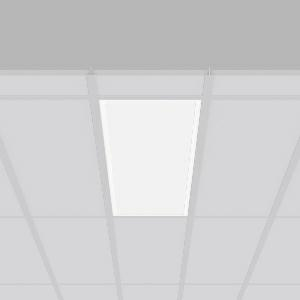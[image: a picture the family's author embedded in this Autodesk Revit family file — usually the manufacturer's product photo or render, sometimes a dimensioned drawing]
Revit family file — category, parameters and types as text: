
# Revit family: sidelite_eco_672372_002_1_04_6a0e
name_source: partatom
category: Lighting Fixtures
units: mm (PartAtom-declared; Revit-internal decimal feet)

## family parameters
Cut with Voids When Loaded = No
Host = Face
Light Source = No
Part Type = Normal
Room Calculation Point = No
Round Connector Dimension = Use Diameter
Shared = No

## types (1)
- SIDELITE ECO (1 x LED Modul 840, 3550 lm, 4000)
    Apparent Load = 29 VA
    CIE Flux Codes = 46 79 96 100 100
    Color Rendering = 80
    Color Temperature = 4000
    Default Elevation = 1800 mm
    Description = Series: SIDELITE ECO
Highly economical recessed luminaire with progressive LED technology. For escape route illumination. Frame made of aluminium, powder-coated. Diffuser: plastic, opal. Lightguide and diffuser made of non-yellowing plastic (PMMA). Lateral light emission (RZB SIDELITE technology) for homogeneous light distribution. External driver. Self-contained system with automatic self-test and feedback to the RZB monitoring system MULTIDIGIT. External driver with simple plug-in locking system. Extended connection cable (1.90 m). 
Colour: white
Length: 1195 mm
Width: 295 mm
Cut-out length: 1170 mm
Cut-out width: 270 mm
Recess height: 160 mm
Luminaire: recess height: 40 mm
Weight: 4.4 kg
Operating mode: maintained power mode
Duration time: 8 h
Lamp: LED
Socket: without socket
Colour temperature: 4000K
Colour rendering index (CRI): 80
System power: 29 W
Rated luminous flux: 3550 lm
Luminous flux, emergency: 240 lm
System power, emergency: -
Control gear: Regulated power supply
Protection class: I
Type of protection: IP 40
    Height = 0 mm  [stored 0 ft]
    Lamp = 1 x LED Modul 840
    Lamp Light Flux = 3550 lm
    Lamp count = 1
    Length = 1195 mm
    Lifetime = 50000 h
    Luminous efficacy = 122 lm/W
    Manufacturer = RZB
    ModVariant = No
    Model = 672372.002.1.04
    Mounting Place = Ceiling
    Mounting Type = Recessed
    Number of Poles = 1
    OnlyDefault = Yes
    Power Factor = 1
    Product Name = SIDELITE ECO
    Product group = Recessed modular luminaires
    ProductGroupID = 406
    Protection Class = Protection class I
    Protection Degree = IP 40
    RLX_Detail_Level = 1
    RLX_Emergency_Light_Flux = 240 lm
    RLX_Emergency_Type = 3
    RLX_Emergency_Type_DB = Yes
    RlxData = <blob elided: 30733 chars, md5=03e999d5>
    Socket = socket
    Standby Power = 0 W
    System Light Flux = 3550 lm
    System Power = 29 W
    Type Comments = Product without accessories
    Type Image = 312365.002.jpg
    URL = http://relux.com
    VarID = ---
    Voltage = 230 V
    Voltage Range = 220-240 V
    Weight = 0.00 kg
    Width = 295 mm

note: [stored X ft] marks values corroborated as IEEE doubles in the binary element streams (Revit-internal decimal feet)

## geometry (parser evidence)
native form markers: Blend x4, Sweep x11
no freeform markers — native parametric forms only
